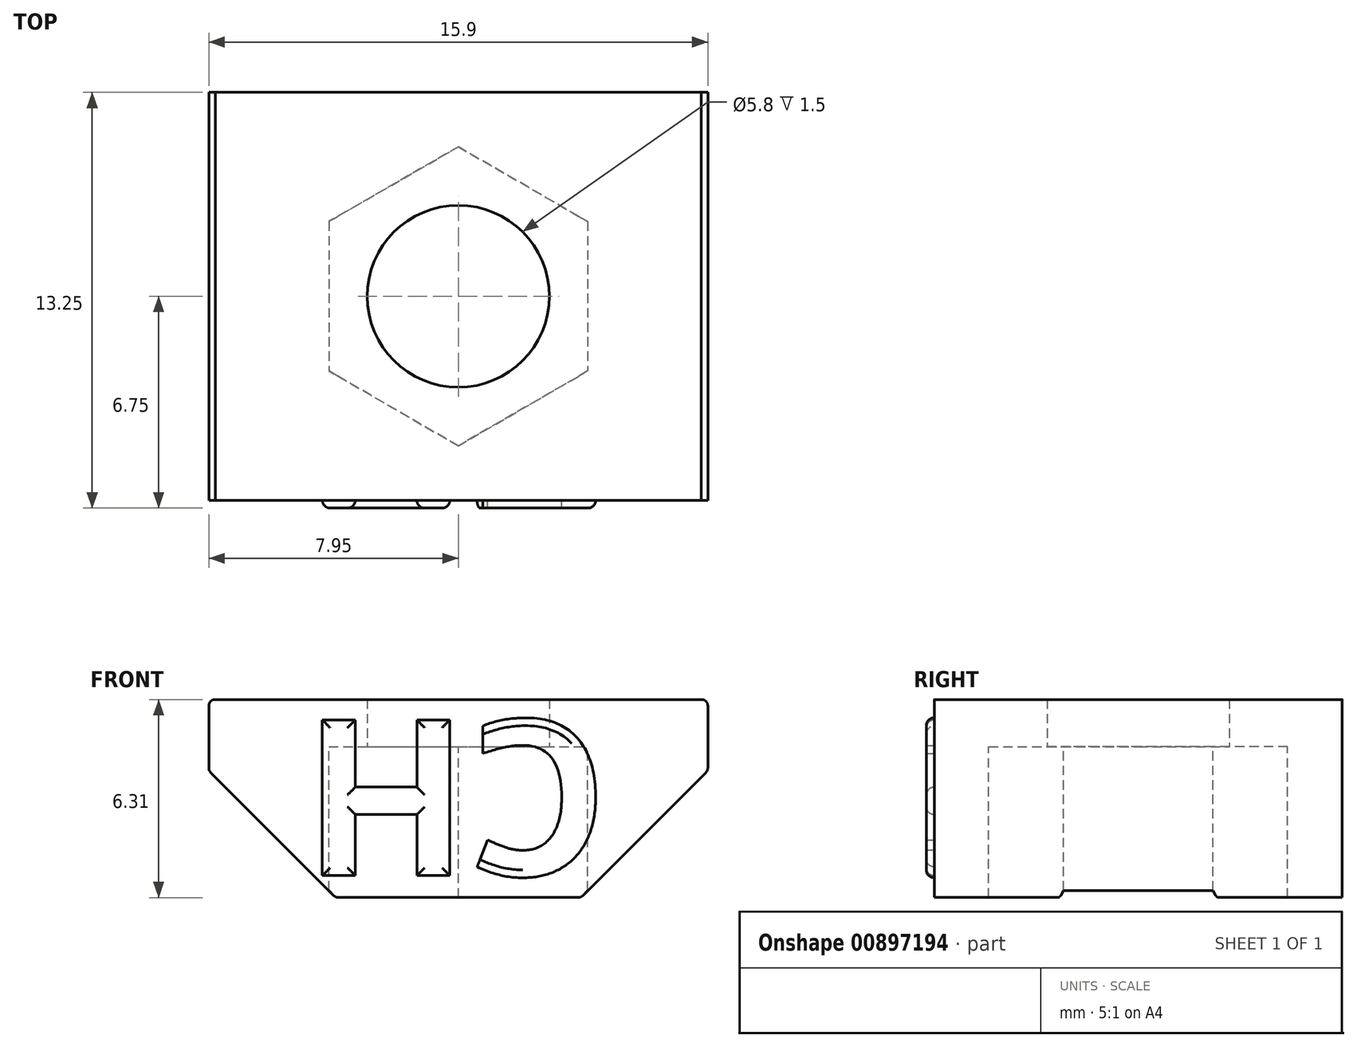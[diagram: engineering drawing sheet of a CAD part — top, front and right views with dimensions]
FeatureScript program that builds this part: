
annotation { "Feature Type Name" : "Feature", "Feature Type Description" : "" }
export const myFeature = defineFeature(function(context is Context, id is Id, definition is map)
    precondition{}
    {
        {
            var Q0;
            Q0=qCreatedBy(makeId("Front.planeOp"),FACE);
            var sketch = newSketch(context, id + "F0", { "sketchPlane" : qUnion([Q0])});
            skArc(sketch, "E0", {"start": v(9.88, 13.7) * mm, "mid": v(9.61, 13.59) * mm, "end": v(9.5, 13.32) * mm});
            skLineSegment(sketch, "E1", {"start": v(12.7, 13.7) * mm, "end": v(9.88, 13.7) * mm});
            skArc(sketch, "E2", {"start": v(13.7, 12.7) * mm, "mid": v(13.4, 13.4) * mm, "end": v(12.7, 13.7) * mm});
            skLineSegment(sketch, "E3", {"start": v(13.7, 9.88) * mm, "end": v(13.7, 12.7) * mm});
            skArc(sketch, "E4", {"start": v(13.32, 9.5) * mm, "mid": v(13.59, 9.61) * mm, "end": v(13.7, 9.88) * mm});
            skLineSegment(sketch, "E5", {"start": v(9.88, 9.5) * mm, "end": v(13.32, 9.5) * mm});
            skArc(sketch, "E6", {"start": v(9.5, 9.88) * mm, "mid": v(9.61, 9.61) * mm, "end": v(9.88, 9.5) * mm});
            skLineSegment(sketch, "E7", {"start": v(9.5, 13.32) * mm, "end": v(9.5, 9.88) * mm});
            skArc(sketch, "E8", {"start": v(-9.5, 13.32) * mm, "mid": v(-9.61, 13.59) * mm, "end": v(-9.88, 13.7) * mm});
            skLineSegment(sketch, "E9", {"start": v(-9.5, 9.88) * mm, "end": v(-9.5, 13.32) * mm});
            skArc(sketch, "E10", {"start": v(-9.88, 9.5) * mm, "mid": v(-9.61, 9.61) * mm, "end": v(-9.5, 9.88) * mm});
            skLineSegment(sketch, "E11", {"start": v(-13.32, 9.5) * mm, "end": v(-9.88, 9.5) * mm});
            skArc(sketch, "E12", {"start": v(-13.7, 9.88) * mm, "mid": v(-13.59, 9.61) * mm, "end": v(-13.32, 9.5) * mm});
            skLineSegment(sketch, "E13", {"start": v(-13.7, 12.7) * mm, "end": v(-13.7, 9.88) * mm});
            skArc(sketch, "E14", {"start": v(-12.7, 13.7) * mm, "mid": v(-13.4, 13.4) * mm, "end": v(-13.7, 12.7) * mm});
            skLineSegment(sketch, "E15", {"start": v(-9.88, 13.7) * mm, "end": v(-12.7, 13.7) * mm});
            skArc(sketch, "E16", {"start": v(-1.5, -3.2) * mm, "mid": v(0, -3.53) * mm, "end": v(1.5, -3.2) * mm});
            skLineSegment(sketch, "E17", {"start": v(-2.47, -3.98) * mm, "end": v(-1.5, -3.2) * mm});
            skArc(sketch, "E18", {"start": v(-3.98, -2.47) * mm, "mid": v(-3.9, -3.9) * mm, "end": v(-2.47, -3.98) * mm});
            skLineSegment(sketch, "E19", {"start": v(-3.2, -1.5) * mm, "end": v(-3.98, -2.47) * mm});
            skArc(sketch, "E20", {"start": v(-3.2, 1.5) * mm, "mid": v(-3.53, 0) * mm, "end": v(-3.2, -1.5) * mm});
            skLineSegment(sketch, "E21", {"start": v(-3.98, 2.47) * mm, "end": v(-3.2, 1.5) * mm});
            skArc(sketch, "E22", {"start": v(-2.47, 3.98) * mm, "mid": v(-3.9, 3.9) * mm, "end": v(-3.98, 2.47) * mm});
            skLineSegment(sketch, "E23", {"start": v(-1.5, 3.2) * mm, "end": v(-2.47, 3.98) * mm});
            skArc(sketch, "E24", {"start": v(1.5, 3.2) * mm, "mid": v(0, 3.53) * mm, "end": v(-1.5, 3.2) * mm});
            skLineSegment(sketch, "E25", {"start": v(2.47, 3.98) * mm, "end": v(1.5, 3.2) * mm});
            skArc(sketch, "E26", {"start": v(3.98, 2.47) * mm, "mid": v(3.9, 3.9) * mm, "end": v(2.47, 3.98) * mm});
            skLineSegment(sketch, "E27", {"start": v(3.2, 1.5) * mm, "end": v(3.98, 2.47) * mm});
            skArc(sketch, "E28", {"start": v(3.2, -1.5) * mm, "mid": v(3.53, 0) * mm, "end": v(3.2, 1.5) * mm});
            skLineSegment(sketch, "E29", {"start": v(3.98, -2.47) * mm, "end": v(3.2, -1.5) * mm});
            skArc(sketch, "E30", {"start": v(2.47, -3.98) * mm, "mid": v(3.9, -3.9) * mm, "end": v(3.98, -2.47) * mm});
            skLineSegment(sketch, "E31", {"start": v(1.5, -3.2) * mm, "end": v(2.47, -3.98) * mm});
            skArc(sketch, "E32", {"start": v(-13.32, -9.5) * mm, "mid": v(-13.59, -9.61) * mm, "end": v(-13.7, -9.88) * mm});
            skLineSegment(sketch, "E33", {"start": v(-9.88, -9.5) * mm, "end": v(-13.32, -9.5) * mm});
            skArc(sketch, "E34", {"start": v(-9.5, -9.88) * mm, "mid": v(-9.61, -9.61) * mm, "end": v(-9.88, -9.5) * mm});
            skLineSegment(sketch, "E35", {"start": v(-9.5, -13.32) * mm, "end": v(-9.5, -9.88) * mm});
            skArc(sketch, "E36", {"start": v(-9.88, -13.7) * mm, "mid": v(-9.61, -13.59) * mm, "end": v(-9.5, -13.32) * mm});
            skLineSegment(sketch, "E37", {"start": v(-12.7, -13.7) * mm, "end": v(-9.88, -13.7) * mm});
            skArc(sketch, "E38", {"start": v(-13.7, -12.7) * mm, "mid": v(-13.4, -13.4) * mm, "end": v(-12.7, -13.7) * mm});
            skLineSegment(sketch, "E39", {"start": v(-13.7, -9.88) * mm, "end": v(-13.7, -12.7) * mm});
            skArc(sketch, "E40", {"start": v(9.5, -13.32) * mm, "mid": v(9.61, -13.59) * mm, "end": v(9.88, -13.7) * mm});
            skLineSegment(sketch, "E41", {"start": v(9.5, -9.88) * mm, "end": v(9.5, -13.32) * mm});
            skArc(sketch, "E42", {"start": v(9.88, -9.5) * mm, "mid": v(9.61, -9.61) * mm, "end": v(9.5, -9.88) * mm});
            skLineSegment(sketch, "E43", {"start": v(13.32, -9.5) * mm, "end": v(9.88, -9.5) * mm});
            skArc(sketch, "E44", {"start": v(13.7, -9.88) * mm, "mid": v(13.59, -9.61) * mm, "end": v(13.32, -9.5) * mm});
            skLineSegment(sketch, "E45", {"start": v(13.7, -12.7) * mm, "end": v(13.7, -9.88) * mm});
            skArc(sketch, "E46", {"start": v(12.7, -13.7) * mm, "mid": v(13.4, -13.4) * mm, "end": v(13.7, -12.7) * mm});
            skLineSegment(sketch, "E47", {"start": v(9.88, -13.7) * mm, "end": v(12.7, -13.7) * mm});
            skArc(sketch, "E48", {"start": v(13.24, -4) * mm, "mid": v(12.89, -4.15) * mm, "end": v(12.74, -4.5) * mm});
            skLineSegment(sketch, "E49", {"start": v(12.74, -4.5) * mm, "end": v(12.74, -7.73) * mm});
            skArc(sketch, "E50", {"start": v(12.24, -8.25) * mm, "mid": v(12.6, -8.1) * mm, "end": v(12.74, -7.73) * mm});
            skLineSegment(sketch, "E51", {"start": v(12.24, -8.25) * mm, "end": v(10.26, -8.25) * mm});
            skArc(sketch, "E52", {"start": v(9.9, -8.1) * mm, "mid": v(10.07, -8.21) * mm, "end": v(10.26, -8.25) * mm});
            skLineSegment(sketch, "E53", {"start": v(9.9, -8.1) * mm, "end": v(5.98, -4.18) * mm});
            skArc(sketch, "E54", {"start": v(5.83, -3.82) * mm, "mid": v(5.87, -4.02) * mm, "end": v(5.98, -4.18) * mm});
            skLineSegment(sketch, "E55", {"start": v(5.83, -3.82) * mm, "end": v(5.83, -1.01) * mm});
            skLineSegment(sketch, "E56", {"start": v(5.83, -1.01) * mm, "end": v(5.32, -0.06) * mm});
            skLineSegment(sketch, "E57", {"start": v(5.32, -0.06) * mm, "end": v(5.83, 0.89) * mm});
            skLineSegment(sketch, "E58", {"start": v(5.83, 0.89) * mm, "end": v(5.83, 3.82) * mm});
            skArc(sketch, "E59", {"start": v(5.98, 4.18) * mm, "mid": v(5.87, 4.02) * mm, "end": v(5.83, 3.82) * mm});
            skLineSegment(sketch, "E60", {"start": v(5.98, 4.18) * mm, "end": v(9.9, 8.1) * mm});
            skArc(sketch, "E61", {"start": v(10.26, 8.25) * mm, "mid": v(10.07, 8.21) * mm, "end": v(9.9, 8.1) * mm});
            skLineSegment(sketch, "E62", {"start": v(10.26, 8.25) * mm, "end": v(12.24, 8.25) * mm});
            skArc(sketch, "E63", {"start": v(12.74, 7.73) * mm, "mid": v(12.6, 8.1) * mm, "end": v(12.24, 8.25) * mm});
            skLineSegment(sketch, "E64", {"start": v(12.74, 7.73) * mm, "end": v(12.74, 4.5) * mm});
            skArc(sketch, "E65", {"start": v(12.74, 4.5) * mm, "mid": v(12.89, 4.15) * mm, "end": v(13.24, 4) * mm});
            skLineSegment(sketch, "E66", {"start": v(13.24, 4) * mm, "end": v(14.5, 4) * mm});
            skArc(sketch, "E67", {"start": v(14.5, 4) * mm, "mid": v(14.85, 4.15) * mm, "end": v(15, 4.5) * mm});
            skLineSegment(sketch, "E68", {"start": v(15, 4.5) * mm, "end": v(15, 13) * mm});
            skArc(sketch, "E69", {"start": v(15, 13) * mm, "mid": v(14.41, 14.41) * mm, "end": v(13, 15) * mm});
            skLineSegment(sketch, "E70", {"start": v(13, 15) * mm, "end": v(4.5, 15) * mm});
            skArc(sketch, "E71", {"start": v(4.5, 15) * mm, "mid": v(4.15, 14.85) * mm, "end": v(4, 14.5) * mm});
            skLineSegment(sketch, "E72", {"start": v(4, 14.5) * mm, "end": v(4, 13.24) * mm});
            skArc(sketch, "E73", {"start": v(4, 13.24) * mm, "mid": v(4.15, 12.89) * mm, "end": v(4.5, 12.74) * mm});
            skLineSegment(sketch, "E74", {"start": v(4.5, 12.74) * mm, "end": v(7.73, 12.74) * mm});
            skArc(sketch, "E75", {"start": v(8.25, 12.24) * mm, "mid": v(8.1, 12.6) * mm, "end": v(7.73, 12.74) * mm});
            skLineSegment(sketch, "E76", {"start": v(8.25, 12.24) * mm, "end": v(8.25, 10.26) * mm});
            skArc(sketch, "E77", {"start": v(8.1, 9.9) * mm, "mid": v(8.21, 10.07) * mm, "end": v(8.25, 10.26) * mm});
            skLineSegment(sketch, "E78", {"start": v(8.1, 9.9) * mm, "end": v(4.18, 5.98) * mm});
            skArc(sketch, "E79", {"start": v(3.82, 5.83) * mm, "mid": v(4.02, 5.87) * mm, "end": v(4.18, 5.98) * mm});
            skLineSegment(sketch, "E80", {"start": v(3.82, 5.83) * mm, "end": v(0.95, 5.83) * mm});
            skLineSegment(sketch, "E81", {"start": v(0.95, 5.83) * mm, "end": v(0, 5.32) * mm});
            skLineSegment(sketch, "E82", {"start": v(0, 5.32) * mm, "end": v(-0.95, 5.83) * mm});
            skLineSegment(sketch, "E83", {"start": v(-0.95, 5.83) * mm, "end": v(-3.82, 5.83) * mm});
            skArc(sketch, "E84", {"start": v(-4.18, 5.98) * mm, "mid": v(-4.02, 5.87) * mm, "end": v(-3.82, 5.83) * mm});
            skLineSegment(sketch, "E85", {"start": v(-4.18, 5.98) * mm, "end": v(-8.1, 9.9) * mm});
            skArc(sketch, "E86", {"start": v(-8.25, 10.26) * mm, "mid": v(-8.21, 10.07) * mm, "end": v(-8.1, 9.9) * mm});
            skLineSegment(sketch, "E87", {"start": v(-8.25, 10.26) * mm, "end": v(-8.25, 12.24) * mm});
            skArc(sketch, "E88", {"start": v(-7.73, 12.74) * mm, "mid": v(-8.1, 12.6) * mm, "end": v(-8.25, 12.24) * mm});
            skLineSegment(sketch, "E89", {"start": v(-7.73, 12.74) * mm, "end": v(-4.5, 12.74) * mm});
            skArc(sketch, "E90", {"start": v(-4.5, 12.74) * mm, "mid": v(-4.15, 12.89) * mm, "end": v(-4, 13.24) * mm});
            skLineSegment(sketch, "E91", {"start": v(-4, 13.24) * mm, "end": v(-4, 14.5) * mm});
            skArc(sketch, "E92", {"start": v(-4, 14.5) * mm, "mid": v(-4.15, 14.85) * mm, "end": v(-4.5, 15) * mm});
            skLineSegment(sketch, "E93", {"start": v(-4.5, 15) * mm, "end": v(-13, 15) * mm});
            skArc(sketch, "E94", {"start": v(-13, 15) * mm, "mid": v(-14.41, 14.41) * mm, "end": v(-15, 13) * mm});
            skLineSegment(sketch, "E95", {"start": v(-15, 13) * mm, "end": v(-15, 4.5) * mm});
            skArc(sketch, "E96", {"start": v(-15, 4.5) * mm, "mid": v(-14.85, 4.15) * mm, "end": v(-14.5, 4) * mm});
            skLineSegment(sketch, "E97", {"start": v(-14.5, 4) * mm, "end": v(-13.24, 4) * mm});
            skArc(sketch, "E98", {"start": v(-13.24, 4) * mm, "mid": v(-12.89, 4.15) * mm, "end": v(-12.74, 4.5) * mm});
            skLineSegment(sketch, "E99", {"start": v(-12.74, 4.5) * mm, "end": v(-12.74, 7.73) * mm});
            skArc(sketch, "E100", {"start": v(-12.24, 8.25) * mm, "mid": v(-12.6, 8.1) * mm, "end": v(-12.74, 7.73) * mm});
            skLineSegment(sketch, "E101", {"start": v(-12.24, 8.25) * mm, "end": v(-10.26, 8.25) * mm});
            skArc(sketch, "E102", {"start": v(-9.9, 8.1) * mm, "mid": v(-10.07, 8.21) * mm, "end": v(-10.26, 8.25) * mm});
            skLineSegment(sketch, "E103", {"start": v(-9.9, 8.1) * mm, "end": v(-5.98, 4.18) * mm});
            skArc(sketch, "E104", {"start": v(-5.83, 3.82) * mm, "mid": v(-5.87, 4.02) * mm, "end": v(-5.98, 4.18) * mm});
            skLineSegment(sketch, "E105", {"start": v(-5.83, 3.82) * mm, "end": v(-5.83, 0.89) * mm});
            skLineSegment(sketch, "E106", {"start": v(-5.83, 0.89) * mm, "end": v(-5.32, -0.06) * mm});
            skLineSegment(sketch, "E107", {"start": v(-5.32, -0.06) * mm, "end": v(-5.83, -1.01) * mm});
            skLineSegment(sketch, "E108", {"start": v(-5.83, -1.01) * mm, "end": v(-5.83, -3.82) * mm});
            skArc(sketch, "E109", {"start": v(-5.98, -4.18) * mm, "mid": v(-5.87, -4.02) * mm, "end": v(-5.83, -3.82) * mm});
            skLineSegment(sketch, "E110", {"start": v(-5.98, -4.18) * mm, "end": v(-9.9, -8.1) * mm});
            skArc(sketch, "E111", {"start": v(-10.26, -8.25) * mm, "mid": v(-10.07, -8.21) * mm, "end": v(-9.9, -8.1) * mm});
            skLineSegment(sketch, "E112", {"start": v(-10.26, -8.25) * mm, "end": v(-12.24, -8.25) * mm});
            skArc(sketch, "E113", {"start": v(-12.74, -7.73) * mm, "mid": v(-12.6, -8.1) * mm, "end": v(-12.24, -8.25) * mm});
            skLineSegment(sketch, "E114", {"start": v(-12.74, -7.73) * mm, "end": v(-12.74, -4.5) * mm});
            skArc(sketch, "E115", {"start": v(-12.74, -4.5) * mm, "mid": v(-12.89, -4.15) * mm, "end": v(-13.24, -4) * mm});
            skLineSegment(sketch, "E116", {"start": v(-13.24, -4) * mm, "end": v(-14.5, -4) * mm});
            skArc(sketch, "E117", {"start": v(-14.5, -4) * mm, "mid": v(-14.85, -4.15) * mm, "end": v(-15, -4.5) * mm});
            skLineSegment(sketch, "E118", {"start": v(-15, -4.5) * mm, "end": v(-15, -13) * mm});
            skArc(sketch, "E119", {"start": v(-15, -13) * mm, "mid": v(-14.41, -14.41) * mm, "end": v(-13, -15) * mm});
            skLineSegment(sketch, "E120", {"start": v(-13, -15) * mm, "end": v(-4.5, -15) * mm});
            skArc(sketch, "E121", {"start": v(-4.5, -15) * mm, "mid": v(-4.15, -14.85) * mm, "end": v(-4, -14.5) * mm});
            skLineSegment(sketch, "E122", {"start": v(-4, -14.5) * mm, "end": v(-4, -13.24) * mm});
            skArc(sketch, "E123", {"start": v(-4, -13.24) * mm, "mid": v(-4.15, -12.89) * mm, "end": v(-4.5, -12.74) * mm});
            skLineSegment(sketch, "E124", {"start": v(-4.5, -12.74) * mm, "end": v(-7.73, -12.74) * mm});
            skArc(sketch, "E125", {"start": v(-8.25, -12.24) * mm, "mid": v(-8.1, -12.6) * mm, "end": v(-7.73, -12.74) * mm});
            skLineSegment(sketch, "E126", {"start": v(-8.25, -12.24) * mm, "end": v(-8.25, -10.26) * mm});
            skArc(sketch, "E127", {"start": v(-8.1, -9.9) * mm, "mid": v(-8.21, -10.07) * mm, "end": v(-8.25, -10.26) * mm});
            skLineSegment(sketch, "E128", {"start": v(-8.1, -9.9) * mm, "end": v(-4.18, -5.98) * mm});
            skArc(sketch, "E129", {"start": v(-3.82, -5.83) * mm, "mid": v(-4.02, -5.87) * mm, "end": v(-4.18, -5.98) * mm});
            skLineSegment(sketch, "E130", {"start": v(-3.82, -5.83) * mm, "end": v(-0.95, -5.83) * mm});
            skLineSegment(sketch, "E131", {"start": v(-0.95, -5.83) * mm, "end": v(0, -5.32) * mm});
            skLineSegment(sketch, "E132", {"start": v(0, -5.32) * mm, "end": v(0.95, -5.83) * mm});
            skLineSegment(sketch, "E133", {"start": v(0.95, -5.83) * mm, "end": v(3.82, -5.83) * mm});
            skArc(sketch, "E134", {"start": v(4.18, -5.98) * mm, "mid": v(4.02, -5.87) * mm, "end": v(3.82, -5.83) * mm});
            skLineSegment(sketch, "E135", {"start": v(4.18, -5.98) * mm, "end": v(8.1, -9.9) * mm});
            skArc(sketch, "E136", {"start": v(8.25, -10.26) * mm, "mid": v(8.21, -10.07) * mm, "end": v(8.1, -9.9) * mm});
            skLineSegment(sketch, "E137", {"start": v(8.25, -10.26) * mm, "end": v(8.25, -12.24) * mm});
            skArc(sketch, "E138", {"start": v(7.73, -12.74) * mm, "mid": v(8.1, -12.6) * mm, "end": v(8.25, -12.24) * mm});
            skLineSegment(sketch, "E139", {"start": v(7.73, -12.74) * mm, "end": v(4.5, -12.74) * mm});
            skArc(sketch, "E140", {"start": v(4.5, -12.74) * mm, "mid": v(4.15, -12.89) * mm, "end": v(4, -13.24) * mm});
            skLineSegment(sketch, "E141", {"start": v(4, -13.24) * mm, "end": v(4, -14.5) * mm});
            skArc(sketch, "E142", {"start": v(4, -14.5) * mm, "mid": v(4.15, -14.85) * mm, "end": v(4.5, -15) * mm});
            skLineSegment(sketch, "E143", {"start": v(4.5, -15) * mm, "end": v(13, -15) * mm});
            skArc(sketch, "E144", {"start": v(13, -15) * mm, "mid": v(14.41, -14.41) * mm, "end": v(15, -13) * mm});
            skLineSegment(sketch, "E145", {"start": v(15, -13) * mm, "end": v(15, -4.5) * mm});
            skArc(sketch, "E146", {"start": v(15, -4.5) * mm, "mid": v(14.85, -4.15) * mm, "end": v(14.5, -4) * mm});
            skLineSegment(sketch, "E147", {"start": v(14.5, -4) * mm, "end": v(13.24, -4) * mm});
            skSolve(sketch);
        }
        {
            var Q0;
            Q0=qCreatedBy(makeId("Front.planeOp"),FACE);
            var sketch = newSketch(context, id + "F1", { "sketchPlane" : qUnion([Q0])});
            skLineSegment(sketch, "E148.0", {"start": v(-7.74, 12.44) * mm, "end": v(0, 12.44) * mm});
            skArc(sketch, "E148.1", {"start": v(-7.74, 12.44) * mm, "mid": v(-7.89, 12.39) * mm, "end": v(-7.95, 12.24) * mm});
            skLineSegment(sketch, "E148.2", {"start": v(-7.95, 10.26) * mm, "end": v(-7.95, 12.24) * mm});
            skLineSegment(sketch, "E148.3", {"start": v(0, 6.13) * mm, "end": v(-3.82, 6.13) * mm});
            skArc(sketch, "E148.4", {"start": v(-3.97, 6.2) * mm, "mid": v(-3.9, 6.15) * mm, "end": v(-3.82, 6.13) * mm});
            skLineSegment(sketch, "E148.5", {"start": v(-3.97, 6.2) * mm, "end": v(-7.9, 10.12) * mm});
            skArc(sketch, "E148.6", {"start": v(-7.95, 10.26) * mm, "mid": v(-7.93, 10.18) * mm, "end": v(-7.9, 10.12) * mm});
            skLineSegment(sketch, "E149", {"start": v(0, 0) * mm, "end": v(0, 9.44) * mm, "construction": true});
            skArc(sketch, "E150.MirrorCS", {"start": v(7.95, 10.26) * mm, "mid": v(7.93, 10.18) * mm, "end": v(7.9, 10.12) * mm});
            skArc(sketch, "E151.MirrorCS", {"start": v(3.97, 6.2) * mm, "mid": v(3.9, 6.15) * mm, "end": v(3.82, 6.13) * mm});
            skArc(sketch, "E152.MirrorCS", {"start": v(7.74, 12.44) * mm, "mid": v(7.89, 12.39) * mm, "end": v(7.95, 12.24) * mm});
            skLineSegment(sketch, "E153.MirrorCS", {"start": v(7.95, 10.26) * mm, "end": v(7.95, 12.24) * mm});
            skLineSegment(sketch, "E154.MirrorCS", {"start": v(3.97, 6.2) * mm, "end": v(7.9, 10.12) * mm});
            skLineSegment(sketch, "E155.MirrorCS", {"start": v(0, 6.13) * mm, "end": v(3.82, 6.13) * mm});
            skLineSegment(sketch, "E156.MirrorCS", {"start": v(7.74, 12.44) * mm, "end": v(0, 12.44) * mm});
            skSolve(sketch);
        }
        {
            var Q0;
            Q0 = qSketchRegion(id + "F1", true);
            extrude(context, id + "F2", {"entities" : qUnion([Q0]), "endBound" : BoundingType.SYMMETRIC, "depth" : 13 * mm, "offsetDistance" : 25 * mm});
        }
        {
            var Q0;
            Q0=makeQuery(id+"F2.opExtrude","SWEPT_FACE",FACE,{"disambiguationData":[OSD([sQuery(id+"F1.wireOp",EDGE,"E148.0"),sQuery(id+"F1.wireOp",EDGE,"E156.MirrorCS")])]});
            cPlane(context, id + "F3", {"entities" : qUnion([Q0]), "cplaneType" : CPlaneType.OFFSET, "offset" : 1.5 * mm, "oppositeDirection" : true, "width" : 150 * mm, "height" : 150 * mm});
        }
        {
            var Q0;
            Q0=qCreatedBy(id+"F3.planeOp",FACE);
            var sketch = newSketch(context, id + "F4", { "sketchPlane" : qUnion([Q0])});
            skCircle(sketch, "E157.cCircle", {"center": v(0, 0) * mm, "radius": 4.13 * mm, "construction": true});
            skLineSegment(sketch, "E157.0", {"start": v(0, 4.76) * mm, "end": v(4.13, 2.38) * mm});
            skLineSegment(sketch, "E157.1", {"start": v(4.12, 2.38) * mm, "end": v(4.13, -2.38) * mm});
            skLineSegment(sketch, "E157.2", {"start": v(4.13, -2.38) * mm, "end": v(0, -4.76) * mm});
            skLineSegment(sketch, "E157.3", {"start": v(0, -4.76) * mm, "end": v(-4.12, -2.38) * mm});
            skLineSegment(sketch, "E157.4", {"start": v(-4.12, -2.38) * mm, "end": v(-4.13, 2.38) * mm});
            skLineSegment(sketch, "E157.5", {"start": v(-4.12, 2.38) * mm, "end": v(0, 4.76) * mm});
            skPoint(sketch, "E157.0.midPoint", {"position": v(2.06, 3.57) * mm});
            skSolve(sketch);
        }
        {
            var Q0;
            Q0 = qSketchRegion(id + "F4", true);
            extrude(context, id + "F5", {"entities" : qUnion([Q0]), "operationType" : NewBodyOperationType.REMOVE, "endBound" : BoundingType.THROUGH_ALL, "oppositeDirection" : true, "depth" : 25 * mm, "offsetDistance" : 25 * mm});
        }
        {
            var Q0;
            Q0=sQuery(id+"F4.wireOp",VERTEX,"E157.cCircle.center");
            var Q1;
            Q1=makeQuery(id+"F2.opExtrude","SWEPT_BODY",BODY,{"disambiguationData":[OSD([sQuery(id+"F1.wireOp",EDGE,"E148.0"),sQuery(id+"F1.wireOp",EDGE,"E148.1"),sQuery(id+"F1.wireOp",EDGE,"E148.2"),sQuery(id+"F1.wireOp",EDGE,"E148.3"),sQuery(id+"F1.wireOp",EDGE,"E148.4"),sQuery(id+"F1.wireOp",EDGE,"E148.5"),sQuery(id+"F1.wireOp",EDGE,"E148.6"),sQuery(id+"F1.wireOp",EDGE,"E150.MirrorCS"),sQuery(id+"F1.wireOp",EDGE,"E151.MirrorCS"),sQuery(id+"F1.wireOp",EDGE,"E152.MirrorCS"),sQuery(id+"F1.wireOp",EDGE,"E153.MirrorCS"),sQuery(id+"F1.wireOp",EDGE,"E154.MirrorCS"),sQuery(id+"F1.wireOp",EDGE,"E155.MirrorCS"),sQuery(id+"F1.wireOp",EDGE,"E156.MirrorCS")])]});
            hole(context, id + "F6", {"style" : HoleStyle.SIMPLE, "endStyle" : HoleEndStyle.THROUGH, "oppositeDirection" : true, "standardTappedOrClearance" : lookupTablePath({ "fit" : "Loose", "standard" : "ISO", "size" : "M5", "type" : "Clearance" }), "standardBlindInLast" : lookupTablePath({ "fit" : "Loose", "standard" : "ISO", "size" : "M5", "type" : "Clearance" }), "holeDiameter" : 5.8 * mm, "majorDiameter" : 5 * mm, "isTappedThrough" : true, "tappedDepth" : 18.5 * mm, "tapClearance" : 3, "locations" : qUnion([Q0]), "scope" : qUnion([Q1])});
        }
        {
            var Q0;
            Q0=makeQuery(id+"F2.opExtrude","CAP_FACE",FACE,{"disambiguationData":[OSD([sQuery(id+"F1.wireOp",EDGE,"E148.0"),sQuery(id+"F1.wireOp",EDGE,"E148.1"),sQuery(id+"F1.wireOp",EDGE,"E148.2"),sQuery(id+"F1.wireOp",EDGE,"E148.3"),sQuery(id+"F1.wireOp",EDGE,"E148.4"),sQuery(id+"F1.wireOp",EDGE,"E148.5"),sQuery(id+"F1.wireOp",EDGE,"E148.6"),sQuery(id+"F1.wireOp",EDGE,"E150.MirrorCS"),sQuery(id+"F1.wireOp",EDGE,"E151.MirrorCS"),sQuery(id+"F1.wireOp",EDGE,"E152.MirrorCS"),sQuery(id+"F1.wireOp",EDGE,"E153.MirrorCS"),sQuery(id+"F1.wireOp",EDGE,"E154.MirrorCS"),sQuery(id+"F1.wireOp",EDGE,"E155.MirrorCS"),sQuery(id+"F1.wireOp",EDGE,"E156.MirrorCS")])],"isStart":false});
            var sketch = newSketch(context, id + "F7", { "sketchPlane" : qUnion([Q0])});
            skText(sketch, "E158", { "text": "CH", "fontName": "OpenSans-Bold.ttf"});
            skLineSegment(sketch, "E159", {"start": v(0, 6.13) * mm, "end": v(0, 6.79) * mm, "construction": true});
            skLineSegment(sketch, "E160", {"start": v(0, 11.79) * mm, "end": v(0, 12.44) * mm, "construction": true});
            const initialGuessF7  = {"E158": [0.00478, 0.01179, -1, 0, 0.005]};
            skSetInitialGuess(sketch, initialGuessF7);
            skSolve(sketch);
        }
        {
            var Q0;
            Q0 = qSketchRegion(id + "F7", true);
            extrude(context, id + "F8", {"entities" : qUnion([Q0]), "operationType" : NewBodyOperationType.ADD, "depth" : .25 * mm, "offsetDistance" : 25 * mm});
        }
        {
            var Q0;
            Q0=makeQuery(id+"F8.opExtrude","CAP_EDGE",EDGE,{"disambiguationData":[OSD([sQuery(id+"F7.wireOp",EDGE,"E158.sketch_text.stroke-10")])],"isStart":false});
            var Q1;
            Q1=makeQuery(id+"F8.opExtrude","CAP_EDGE",EDGE,{"disambiguationData":[OSD([sQuery(id+"F7.wireOp",EDGE,"E158.sketch_text.stroke-21")])],"isStart":false});
            var Q2;
            Q2=makeQuery(id+"F8.opExtrude","CAP_EDGE",EDGE,{"disambiguationData":[OSD([sQuery(id+"F7.wireOp",EDGE,"E158.sketch_text.stroke-25")])],"isStart":false});
            var Q3;
            Q3=makeQuery(id+"F8.opExtrude","CAP_EDGE",EDGE,{"disambiguationData":[OSD([sQuery(id+"F7.wireOp",EDGE,"E158.sketch_text.stroke-23")])],"isStart":false});
            var Q4;
            Q4=makeQuery(id+"F8.opExtrude","CAP_EDGE",EDGE,{"disambiguationData":[OSD([sQuery(id+"F7.wireOp",EDGE,"E158.sketch_text.stroke-24")])],"isStart":false});
            var Q5;
            Q5=makeQuery(id+"F8.opExtrude","CAP_EDGE",EDGE,{"disambiguationData":[OSD([sQuery(id+"F7.wireOp",EDGE,"E158.sketch_text.stroke-22")])],"isStart":false});
            var Q6;
            Q6=makeQuery(id+"F8.opExtrude","CAP_EDGE",EDGE,{"disambiguationData":[OSD([sQuery(id+"F7.wireOp",EDGE,"E158.sketch_text.stroke-26")])],"isStart":false});
            var Q7;
            Q7=makeQuery(id+"F8.opExtrude","CAP_EDGE",EDGE,{"disambiguationData":[OSD([sQuery(id+"F7.wireOp",EDGE,"E158.sketch_text.stroke-15")])],"isStart":false});
            var Q8;
            Q8=makeQuery(id+"F8.opExtrude","CAP_EDGE",EDGE,{"disambiguationData":[OSD([sQuery(id+"F7.wireOp",EDGE,"E158.sketch_text.stroke-16")])],"isStart":false});
            var Q9;
            Q9=makeQuery(id+"F8.opExtrude","CAP_EDGE",EDGE,{"disambiguationData":[OSD([sQuery(id+"F7.wireOp",EDGE,"E158.sketch_text.stroke-17")])],"isStart":false});
            var Q10;
            Q10=makeQuery(id+"F8.opExtrude","CAP_EDGE",EDGE,{"disambiguationData":[OSD([sQuery(id+"F7.wireOp",EDGE,"E158.sketch_text.stroke-18")])],"isStart":false});
            var Q11;
            Q11=makeQuery(id+"F8.opExtrude","CAP_EDGE",EDGE,{"disambiguationData":[OSD([sQuery(id+"F7.wireOp",EDGE,"E158.sketch_text.stroke-19")])],"isStart":false});
            var Q12;
            Q12=makeQuery(id+"F8.opExtrude","CAP_EDGE",EDGE,{"disambiguationData":[OSD([sQuery(id+"F7.wireOp",EDGE,"E158.sketch_text.stroke-20")])],"isStart":false});
            fillet(context, id + "F9", {"entities" : qUnion([Q0, Q1, Q2, Q3, Q4, Q5, Q6, Q7, Q8, Q9, Q10, Q11, Q12]), "radius" : .25 * mm, "tangentPropagation" : true, "allowEdgeOverflow" : false});
        }
    });
